# Revit family: FU_Modular_Sandler_Cosmo 1515
name_source: partatom
category: Furniture
units: mm (PartAtom-declared; Revit-internal decimal feet)

## family parameters
Always vertical = Yes
Cut with Voids When Loaded = No
OmniClass Number = 23.40.20.00
OmniClass Title = General Furniture and Specialties
Room Calculation Point = No
Shared = No
Work Plane-Based = No

## types (1)
- Cosmo 1515
    Default Elevation = 0 mm  [stored 0 ft]
    Depth = 340 mm  [stored 1.11549 ft]
    Description = A convenient side table in the Cosmo range of modular lounge furniture. HPL laminate table top. Steel frame with a range of color options.
    Height = 600 mm
    Manufacturer = Sandler
    Model = Cosmo 1515
    URL = https://www.sandlerseating.com
    Width = 430 mm  [stored 1.41076 ft]

note: [stored X ft] marks values corroborated as IEEE doubles in the binary element streams (Revit-internal decimal feet)

## geometry (parser evidence)
native form markers: Sweep x3
no freeform markers — native parametric forms only
